# Revit family: ПЛ-10
name_source: partatom
category: Оборудование
units: mm (PartAtom-declared; Revit-internal decimal feet)

## family parameters
Всегда вертикально = Да
Классификация = Нет
На основе рабочей плоскости = Нет
Общий = Нет
При загрузке вырезать с полостями = Нет
Размер круглого соединителя = Использовать диаметр
Тип детали = Нормальный
Точка принадлежности помещению = Нет

## types (22) — shared parameters
00_20_Manufacturer = Вентс
00_20_Name = Клапан протипожежний вогнезатримувальний
Grid Material = Cover Grid Cross
Load Classification = HVAC
Maintenance zone material = <По категории>
Number of Fase = 1
Power = 7 В·А
Voltage = 230 В
zero-valued in all types: Отметка по умолчанию

## per-type parameters (varying)
| type | B | D | D1 | D2 | L | Maximum Air Flow | R | Вес |
| ПЛ-10-ПВП230Т-ДН100/ЕІ60 | 195 мм | 99 мм | 100 мм | 95 мм | 300 мм | 9000.0 л/с | 50 мм | 2.9 кг |
| ПЛ-10-ПВП230Т-ДН400/ЕІ60 | 505 мм | 399 мм | 400 мм | 395 мм | 310 мм | 0.0 л/с | 200 мм | 9.9 кг |
| ПЛ-10-ПВП230Т-ДН100/ЕІ120 | 195 мм | 99 мм | 100 мм | 95 мм | 300 мм | 0.0 л/с | 50 мм | 2.9 кг |
| ПЛ-10-ПВП230Т-ДН400/ЕІ120 | 505 мм | 399 мм | 400 мм | 395 мм | 310 мм | 0.0 л/с | 200 мм | 9.9 кг |
| ПЛ-10-ПВП230Т-ДН125/ЕІ60 | 215 мм | 124 мм | 125 мм | 120 мм | 300 мм | 0.0 л/с | 62 мм | 3.1 кг |
| ПЛ-10-ПВП230Т-ДН125/ЕІ120 | 215 мм | 124 мм | 125 мм | 120 мм | 300 мм | 0.0 л/с | 62 мм | 3.1 кг |
| ПЛ-10-ПВП230Т-ДН150/ЕІ60 | 245 мм | 149 мм | 150 мм | 145 мм | 300 мм | 0.0 л/с | 75 мм | 3.4 кг |
| ПЛ-10-ПВП230Т-ДН150/ЕІ120 | 245 мм | 149 мм | 150 мм | 145 мм | 300 мм | 0.0 л/с | 75 мм | 3.4 кг |
| ПЛ-10-ПВП230Т-ДН160/ЕІ120 | 255 мм | 159 мм | 160 мм | 155 мм | 300 мм | 0.0 л/с | 80 мм | 3.5 кг |
| ПЛ-10-ПВП230Т-ДН180/ЕІ120 | 275 мм | 179 мм | 180 мм | 175 мм | 300 мм | 0.0 л/с | 90 мм | 3.8 кг |
| ПЛ-10-ПВП230Т-ДН160/ЕІ60 | 255 мм | 159 мм | 160 мм | 155 мм | 300 мм | 0.0 л/с | 80 мм | 3.5 кг |
| ПЛ-10-ПВП230Т-ДН180/ЕІ60 | 275 мм | 179 мм | 180 мм | 175 мм | 300 мм | 0.0 л/с | 90 мм | 3.8 кг |
| ПЛ-10-ПВП230Т-ДН200/ЕІ120 | 295 мм | 199 мм | 200 мм | 195 мм | 300 мм | 0.0 л/с | 100 мм | 4 кг |
| ПЛ-10-ПВП230Т-ДН200/ЕІ60 | 295 мм | 199 мм | 200 мм | 195 мм | 300 мм | 0.0 л/с | 100 мм | 4 кг |
| ПЛ-10-ПВП230Т-ДН225/ЕІ120 | 325 мм | 224 мм | 225 мм | 220 мм | 300 мм | 0.0 л/с | 112 мм | 4.4 кг |
| ПЛ-10-ПВП230Т-ДН225/ЕІ60 | 325 мм | 224 мм | 225 мм | 220 мм | 300 мм | 0.0 л/с | 112 мм | 4.4 кг |
| ПЛ-10-ПВП230Т-ДН250/ЕІ120 | 345 мм | 249 мм | 250 мм | 245 мм | 310 мм | 0.0 л/с | 125 мм | 4.7 кг |
| ПЛ-10-ПВП230Т-ДН250/ЕІ60 | 345 мм | 249 мм | 250 мм | 245 мм | 310 мм | 0.0 л/с | 125 мм | 4.7 кг |
| ПЛ-10-ПВП230Т-ДН315/ЕІ120 | 415 мм | 314 мм | 315 мм | 310 мм | 310 мм | 0.0 л/с | 157 мм | 6.5 кг |
| ПЛ-10-ПВП230Т-ДН315/ЕІ60 | 415 мм | 314 мм | 315 мм | 310 мм | 310 мм | 0.0 л/с | 157 мм | 6.5 кг |
| ПЛ-10-ПВП230Т-ДН355/ЕІ120 | 455 мм | 354 мм | 355 мм | 350 мм | 310 мм | 0.0 л/с | 177 мм | 8.3 кг |
| ПЛ-10-ПВП230Т-ДН355/ЕІ60 | 455 мм | 354 мм | 355 мм | 350 мм | 310 мм | 0.0 л/с | 177 мм | 8.3 кг |

note: column(s) folded — value = type name in every type: 00_20_Type
